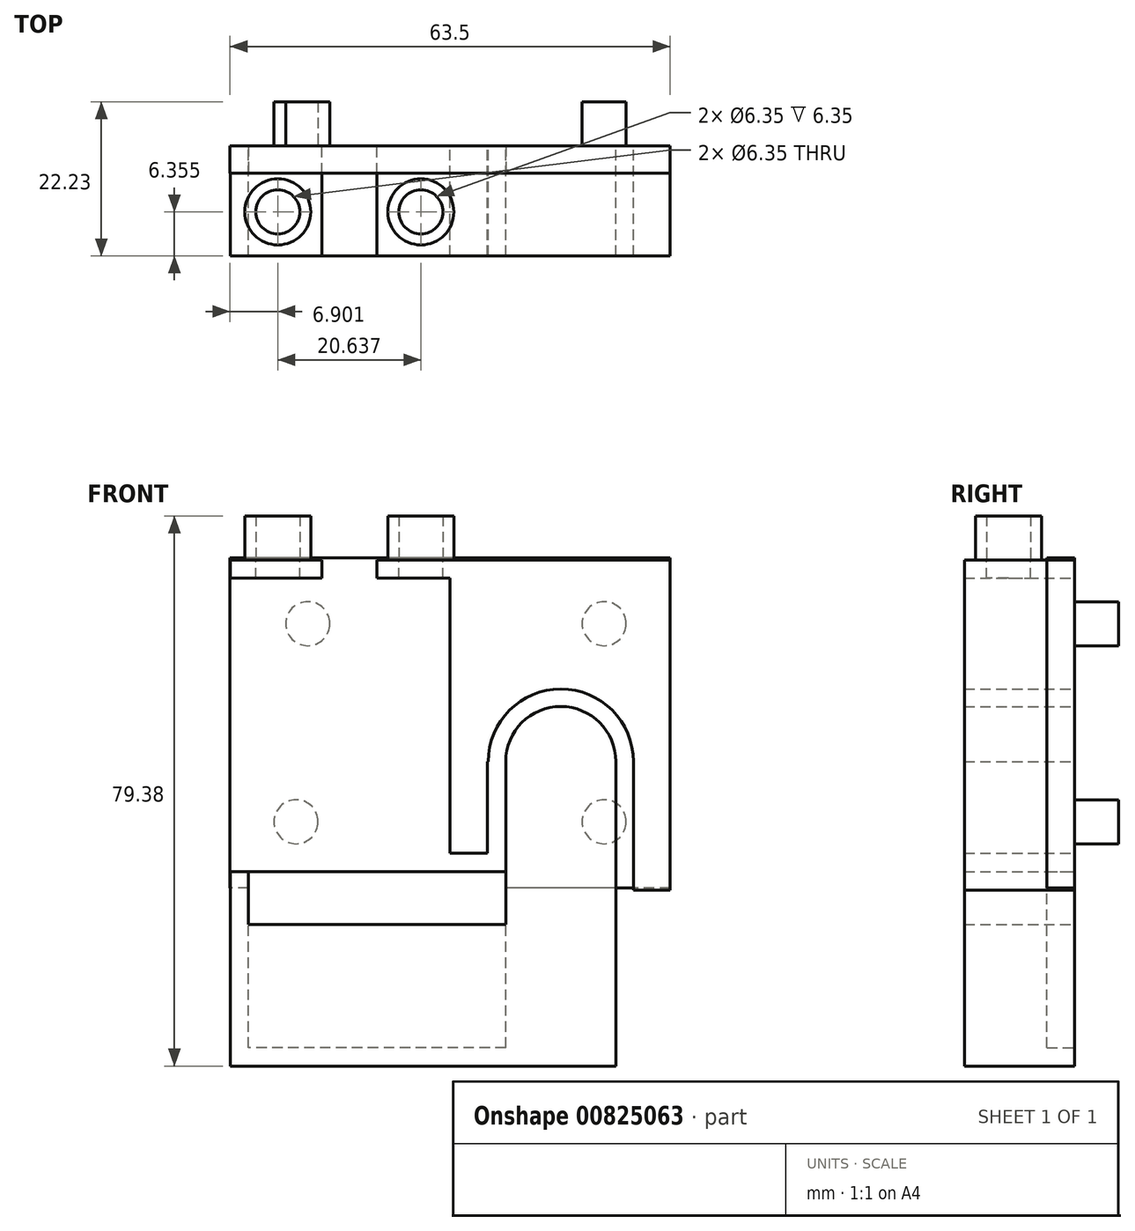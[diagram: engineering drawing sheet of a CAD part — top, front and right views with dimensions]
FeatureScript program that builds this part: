
annotation { "Feature Type Name" : "Feature", "Feature Type Description" : "" }
export const myFeature = defineFeature(function(context is Context, id is Id, definition is map)
    precondition{}
    {
        {
            var Q0;
            Q0=qCreatedBy(makeId("Front.planeOp"),FACE);
            var sketch = newSketch(context, id + "F0", { "sketchPlane" : qUnion([Q0])});
            skLineSegment(sketch, "E0.bottom", {"start": v(-31.75, 44.98) * mm, "end": v(0, 44.98) * mm});
            skLineSegment(sketch, "E0.top", {"start": v(-31.75, 0) * mm, "end": v(0, 0) * mm});
            skLineSegment(sketch, "E0.left", {"start": v(-31.75, 44.98) * mm, "end": v(-31.75, 0) * mm});
            skLineSegment(sketch, "E0.right", {"start": v(0, 44.98) * mm, "end": v(0, 0) * mm});
            skLineSegment(sketch, "E1.bottom", {"start": v(-26.35, 0) * mm, "end": v(-23.7, 0) * mm});
            skLineSegment(sketch, "E1.top", {"start": v(-26.35, 15.88) * mm, "end": v(-23.7, 15.88) * mm});
            skLineSegment(sketch, "E1.left", {"start": v(-26.35, 0) * mm, "end": v(-26.35, 15.87) * mm});
            skLineSegment(sketch, "E1.right", {"start": v(-23.7, 0) * mm, "end": v(-23.7, 15.87) * mm});
            skLineSegment(sketch, "E2.bottom", {"start": v(-7.83, 0) * mm, "end": v(-5.3, 0) * mm});
            skLineSegment(sketch, "E2.top", {"start": v(-7.83, 15.88) * mm, "end": v(-5.3, 15.88) * mm});
            skLineSegment(sketch, "E2.left", {"start": v(-7.83, 0) * mm, "end": v(-7.83, 15.87) * mm});
            skLineSegment(sketch, "E2.right", {"start": v(-5.3, 0) * mm, "end": v(-5.3, 15.87) * mm});
            skArc(sketch, "E3", {"start": v(-5.3, 15.87) * mm, "mid": v(-15.77, 26.35) * mm, "end": v(-26.25, 15.87) * mm});
            skArc(sketch, "E4", {"start": v(-7.83, 15.87) * mm, "mid": v(-15.77, 23.81) * mm, "end": v(-23.7, 15.87) * mm});
            skLineSegment(sketch, "E5.bottom", {"start": v(-26.35, 0) * mm, "end": v(-31.75, 0) * mm});
            skLineSegment(sketch, "E5.top", {"start": v(-26.35, 2.65) * mm, "end": v(-31.75, 2.65) * mm});
            skLineSegment(sketch, "E5.left", {"start": v(-26.35, 0) * mm, "end": v(-26.35, 2.65) * mm});
            skLineSegment(sketch, "E5.right", {"start": v(-31.75, 0) * mm, "end": v(-31.75, 2.65) * mm});
            skLineSegment(sketch, "E6.bottom", {"start": v(-31.75, 44.98) * mm, "end": v(-63.47, 44.98) * mm});
            skLineSegment(sketch, "E6.top", {"start": v(-31.75, 42.34) * mm, "end": v(-63.47, 42.34) * mm});
            skLineSegment(sketch, "E6.left", {"start": v(-31.75, 44.98) * mm, "end": v(-31.75, 42.34) * mm});
            skLineSegment(sketch, "E6.right", {"start": v(-63.47, 44.98) * mm, "end": v(-63.47, 42.34) * mm});
            skLineSegment(sketch, "E7.bottom", {"start": v(-63.47, 42.34) * mm, "end": v(-60.82, 42.34) * mm});
            skLineSegment(sketch, "E7.top", {"start": v(-63.47, 0) * mm, "end": v(-60.82, 0) * mm});
            skLineSegment(sketch, "E7.left", {"start": v(-63.47, 42.34) * mm, "end": v(-63.47, 0) * mm});
            skLineSegment(sketch, "E7.right", {"start": v(-60.82, 42.34) * mm, "end": v(-60.82, 0) * mm});
            skLineSegment(sketch, "E8.bottom", {"start": v(-63.47, 0) * mm, "end": v(0, 0) * mm});
            skLineSegment(sketch, "E8.top", {"start": v(-63.47, -2.65) * mm, "end": v(0, -2.65) * mm});
            skLineSegment(sketch, "E8.left", {"start": v(-63.47, 0) * mm, "end": v(-63.47, -2.65) * mm});
            skLineSegment(sketch, "E8.right", {"start": v(0, 0) * mm, "end": v(0, -2.65) * mm});
            skLineSegment(sketch, "E9.top", {"start": v(-7.83, -2.65) * mm, "end": v(-5.3, -2.65) * mm});
            skLineSegment(sketch, "E9.left", {"start": v(-7.83, 0) * mm, "end": v(-7.83, -2.65) * mm});
            skLineSegment(sketch, "E9.right", {"start": v(-5.3, 0) * mm, "end": v(-5.3, -2.65) * mm});
            skLineSegment(sketch, "E10.bottom", {"start": v(-58.18, 44.98) * mm, "end": v(-55.53, 44.98) * mm});
            skLineSegment(sketch, "E10.top", {"start": v(-58.18, 42.34) * mm, "end": v(-55.53, 42.34) * mm});
            skLineSegment(sketch, "E11.bottom", {"start": v(-50.25, 44.98) * mm, "end": v(-42.31, 44.98) * mm});
            skLineSegment(sketch, "E11.top", {"start": v(-50.25, 42.34) * mm, "end": v(-42.31, 42.34) * mm});
            skLineSegment(sketch, "E11.left", {"start": v(-50.25, 44.98) * mm, "end": v(-50.25, 42.34) * mm});
            skLineSegment(sketch, "E11.right", {"start": v(-42.31, 44.98) * mm, "end": v(-42.31, 42.34) * mm});
            skLineSegment(sketch, "E12.bottom", {"start": v(-37.04, 44.98) * mm, "end": v(-34.4, 44.98) * mm});
            skLineSegment(sketch, "E12.top", {"start": v(-37.04, 42.34) * mm, "end": v(-34.4, 42.34) * mm});
            skSolve(sketch);
        }
        {
            var Q0;
            Q0=makeQuery(id+"F0.imprint","IMPRINT",FACE,{"disambiguationData":[TD([[makeQuery(id+"F0.imprint","IMPRINT",EDGE,{"derivedFrom":sQuery(id+"F0.wireOp",EDGE,"E0.bottom")}),-1.0]])]});
            var Q1;
            {var subQ0=sQuery(id+"F0.wireOp",EDGE,"E1.right");Q1=makeQuery(id+"F0.imprint","IMPRINT",FACE,{"disambiguationData":[TD([[makeQuery(id+"F0.imprint","IMPRINT",EDGE,{"derivedFrom":subQ0}),-1.0]])]});}
            var Q2;
            {var subQ6=sQuery(id+"F0.wireOp",EDGE,"E8.left");Q2=makeQuery(id+"F0.imprint","IMPRINT",FACE,{"disambiguationData":[TD([[makeQuery(id+"F0.imprint","IMPRINT",EDGE,{"derivedFrom":subQ6}),1.0]])]});}
            var Q3;
            {var subQ0=sQuery(id+"F0.wireOp",EDGE,"E8.right");Q3=makeQuery(id+"F0.imprint","IMPRINT",FACE,{"disambiguationData":[TD([[makeQuery(id+"F0.imprint","IMPRINT",EDGE,{"derivedFrom":subQ0}),-1.0]])]});}
            var Q4;
            Q4=makeQuery(id+"F0.imprint","IMPRINT",FACE,{"disambiguationData":[TD([[makeQuery(id+"F0.imprint","IMPRINT",EDGE,{"derivedFrom":sQuery(id+"F0.wireOp",EDGE,"E7.bottom")}),-1.0]])]});
            var Q5;
            {var subQ1=sQuery(id+"F0.wireOp",EDGE,"E6.right");Q5=makeQuery(id+"F0.imprint","IMPRINT",FACE,{"disambiguationData":[TD([[makeQuery(id+"F0.imprint","IMPRINT",EDGE,{"derivedFrom":subQ1}),1.0]])]});}
            var Q6;
            {var subQ0=sQuery(id+"F0.wireOp",EDGE,"E10.right");Q6=makeQuery(id+"F0.imprint","IMPRINT",FACE,{"disambiguationData":[TD([[makeQuery(id+"F0.imprint","IMPRINT",EDGE,{"derivedFrom":subQ0}),1.0]])]});}
            var Q7;
            {var subQ0=sQuery(id+"F0.wireOp",EDGE,"E11.right");Q7=makeQuery(id+"F0.imprint","IMPRINT",FACE,{"disambiguationData":[TD([[makeQuery(id+"F0.imprint","IMPRINT",EDGE,{"derivedFrom":subQ0}),1.0]])]});}
            var Q8;
            {var subQ0=sQuery(id+"F0.wireOp",EDGE,"E6.left");Q8=makeQuery(id+"F0.imprint","IMPRINT",FACE,{"disambiguationData":[TD([[makeQuery(id+"F0.imprint","IMPRINT",EDGE,{"derivedFrom":subQ0}),-1.0]])]});}
            extrude(context, id + "F1", {"entities" : qUnion([Q0, Q1, Q2, Q3, Q4, Q5, Q6, Q7, Q8]), "depth" : 15.88 * mm, "offsetDistance" : 25.4 * mm});
        }
        {
            var Q0;
            Q0=qCreatedBy(makeId("Front.planeOp"),FACE);
            var sketch = newSketch(context, id + "F2", { "sketchPlane" : qUnion([Q0])});
            skLineSegment(sketch, "E13.bottom", {"start": v(0, 45.3) * mm, "end": v(-63.5, 45.3) * mm});
            skLineSegment(sketch, "E13.top", {"start": v(0, -2.33) * mm, "end": v(-63.5, -2.33) * mm});
            skLineSegment(sketch, "E13.left", {"start": v(0, 45.3) * mm, "end": v(0, -2.33) * mm});
            skLineSegment(sketch, "E13.right", {"start": v(-63.5, 45.3) * mm, "end": v(-63.5, -2.33) * mm});
            skCircle(sketch, "E14", {"center": v(-9.53, 35.77) * mm, "radius": 3.18 * mm});
            skCircle(sketch, "E15", {"center": v(-52.28, 35.77) * mm, "radius": 3.18 * mm});
            skCircle(sketch, "E16", {"center": v(-53.97, 7.2) * mm, "radius": 3.18 * mm});
            skCircle(sketch, "E17", {"center": v(-9.52, 7.2) * mm, "radius": 3.18 * mm});
            skSolve(sketch);
        }
        {
            var Q0;
            Q0=qSketchRegion(id+"F2",true);
            var Q1;
            Q1=makeQuery(id+"F2.imprint","IMPRINT",FACE,{"disambiguationData":[TD([[makeQuery(id+"F2.imprint","IMPRINT",EDGE,{"derivedFrom":sQuery(id+"F2.wireOp",EDGE,"E15")}),1.0]])]});
            var Q2;
            Q2=makeQuery(id+"F2.imprint","IMPRINT",FACE,{"disambiguationData":[TD([[makeQuery(id+"F2.imprint","IMPRINT",EDGE,{"derivedFrom":sQuery(id+"F2.wireOp",EDGE,"E16")}),1.0]])]});
            var Q3;
            Q3=makeQuery(id+"F2.imprint","IMPRINT",FACE,{"disambiguationData":[TD([[makeQuery(id+"F2.imprint","IMPRINT",EDGE,{"derivedFrom":sQuery(id+"F2.wireOp",EDGE,"E17")}),1.0]])]});
            var Q4;
            Q4=makeQuery(id+"F2.imprint","IMPRINT",FACE,{"disambiguationData":[TD([[makeQuery(id+"F2.imprint","IMPRINT",EDGE,{"derivedFrom":sQuery(id+"F2.wireOp",EDGE,"E14")}),1.0]])]});
            extrude(context, id + "F3", {"entities" : qUnion([Q0, Q1, Q2, Q3, Q4]), "depth" : 3.97 * mm, "offsetDistance" : 25.4 * mm});
        }
        {
            var Q0;
            Q0=makeQuery(id+"F2.imprint","IMPRINT",FACE,{"disambiguationData":[TD([[makeQuery(id+"F2.imprint","IMPRINT",EDGE,{"derivedFrom":sQuery(id+"F2.wireOp",EDGE,"E14")}),1.0]])]});
            var Q1;
            Q1=makeQuery(id+"F2.imprint","IMPRINT",FACE,{"disambiguationData":[TD([[makeQuery(id+"F2.imprint","IMPRINT",EDGE,{"derivedFrom":sQuery(id+"F2.wireOp",EDGE,"E15")}),1.0]])]});
            var Q2;
            Q2=makeQuery(id+"F2.imprint","IMPRINT",FACE,{"disambiguationData":[TD([[makeQuery(id+"F2.imprint","IMPRINT",EDGE,{"derivedFrom":sQuery(id+"F2.wireOp",EDGE,"E17")}),1.0]])]});
            var Q3;
            Q3=makeQuery(id+"F2.imprint","IMPRINT",FACE,{"disambiguationData":[TD([[makeQuery(id+"F2.imprint","IMPRINT",EDGE,{"derivedFrom":sQuery(id+"F2.wireOp",EDGE,"E16")}),1.0]])]});
            var Q4;
            Q4=sQuery(id+"F2.wireOp",EDGE,"E14");
            var Q5;
            Q5=sQuery(id+"F2.wireOp",EDGE,"E15");
            var Q6;
            Q6=sQuery(id+"F2.wireOp",EDGE,"E17");
            var Q7;
            Q7=sQuery(id+"F2.wireOp",EDGE,"E16");
            extrude(context, id + "F4", {"entities" : qUnion([Q0, Q1, Q2, Q3]), "surfaceEntities" : qUnion([Q4, Q5, Q6, Q7]), "oppositeDirection" : true, "depth" : 6.35 * mm, "offsetDistance" : 25.4 * mm});
        }
        {
            var Q0;
            Q0=makeQuery(id+"F1.opExtrude","SWEPT_FACE",FACE,{"disambiguationData":[OSD([sQuery(id+"F0.wireOp",EDGE,"E6.bottom"),sQuery(id+"F0.wireOp",EDGE,"E10.bottom")])]});
            var sketch = newSketch(context, id + "F5", { "sketchPlane" : qUnion([Q0])});
            skCircle(sketch, "E18", {"center": v(-56.6, -9.52) * mm, "radius": 3.18 * mm});
            skCircle(sketch, "E19", {"center": v(-35.96, -9.52) * mm, "radius": 3.18 * mm});
            skCircle(sketch, "E20", {"center": v(-56.6, -9.52) * mm, "radius": 4.76 * mm});
            skCircle(sketch, "E21", {"center": v(-35.96, -9.52) * mm, "radius": 4.76 * mm});
            skSolve(sketch);
        }
        {
            var Q0;
            Q0=qSketchRegion(id+"F5",true);
            extrude(context, id + "F6", {"entities" : qUnion([Q0]), "depth" : 6.35 * mm, "offsetDistance" : 25.4 * mm});
        }
        {
            var Q0;
            Q0=makeQuery(id+"F1.opExtrude","SWEPT_FACE",FACE,{"disambiguationData":[OSD([sQuery(id+"F0.wireOp",EDGE,"E6.bottom"),sQuery(id+"F0.wireOp",EDGE,"E10.bottom")])]});
            var sketch = newSketch(context, id + "F7", { "sketchPlane" : qUnion([Q0])});
            skCircle(sketch, "E22", {"center": v(-35.96, -9.52) * mm, "radius": 3.18 * mm});
            skCircle(sketch, "E23", {"center": v(-56.6, -9.52) * mm, "radius": 3.18 * mm});
            skSolve(sketch);
        }
        {
            var Q0;
            Q0=qSketchRegion(id+"F7",true);
            extrude(context, id + "F8", {"entities" : qUnion([Q0]), "operationType" : NewBodyOperationType.REMOVE, "oppositeDirection" : true, "depth" : 25.4 * mm, "offsetDistance" : 25.4 * mm});
        }
        {
            var Q0;
            {var subQ0=sQuery(id+"F0.wireOp",EDGE,"E8.top");Q0=makeQuery(id+"F1.opExtrude","SWEPT_FACE",FACE,{"disambiguationData":[OSD([subQ0]),TDD([makeQuery(id+"F0.imprint","IMPRINT",EDGE,{"disambiguationData":[TD([[makeQuery(id+"F0.imprint","INTERSECT",VERTEX,{"derivedFrom":[subQ0,sQuery(id+"F0.wireOp",EDGE,"E8.left")]}),-1.0]])],"derivedFrom":subQ0})])]});}
            var sketch = newSketch(context, id + "F9", { "sketchPlane" : qUnion([Q0])});
            skLineSegment(sketch, "E24.bottom", {"start": v(-63.47, 0) * mm, "end": v(-7.83, 0) * mm});
            skLineSegment(sketch, "E24.top", {"start": v(-63.47, 15.88) * mm, "end": v(-7.83, 15.88) * mm});
            skLineSegment(sketch, "E24.left", {"start": v(-63.47, 0) * mm, "end": v(-63.47, 15.88) * mm});
            skLineSegment(sketch, "E24.right", {"start": v(-7.83, 0) * mm, "end": v(-7.83, 15.88) * mm});
            skSolve(sketch);
        }
        {
            var Q0;
            Q0=qSketchRegion(id+"F9",true);
            extrude(context, id + "F10", {"entities" : qUnion([Q0]), "operationType" : NewBodyOperationType.ADD, "depth" : 25.4 * mm, "offsetDistance" : 25.4 * mm});
        }
        {
            var Q0;
            {var subQ0=sQuery(id+"F0.wireOp",EDGE,"E8.bottom");var subQ1=makeQuery(id+"F0.imprint","INTERSECT",VERTEX,{"derivedFrom":[sQuery(id+"F0.wireOp",EDGE,"E5.left"),subQ0]});var subQ2=makeQuery(id+"F0.imprint","INTERSECT",VERTEX,{"derivedFrom":[sQuery(id+"F0.wireOp",EDGE,"E5.right"),subQ0]});Q0=makeQuery(id+"F1.opExtrude","SWEPT_FACE",FACE,{"disambiguationData":[OSD([subQ0]),TDD([makeQuery(id+"F0.imprint","IMPRINT",EDGE,{"disambiguationData":[TD([[subQ2,1.0]])],"derivedFrom":subQ0}),makeQuery(id+"F0.imprint","IMPRINT",EDGE,{"disambiguationData":[TD([[subQ1,1.0]])],"derivedFrom":subQ0}),makeQuery(id+"F0.imprint","IMPRINT",EDGE,{"disambiguationData":[TD([[makeQuery(id+"F0.imprint","INTERSECT",VERTEX,{"derivedFrom":[sQuery(id+"F0.wireOp",EDGE,"E1.right"),subQ0]}),1.0]])],"derivedFrom":subQ0})])]});}
            var sketch = newSketch(context, id + "F11", { "sketchPlane" : qUnion([Q0])});
            skLineSegment(sketch, "E25.bottom", {"start": v(-60.82, -15.88) * mm, "end": v(-23.7, -15.88) * mm});
            skLineSegment(sketch, "E25.top", {"start": v(-60.82, 0) * mm, "end": v(-23.7, 0) * mm});
            skLineSegment(sketch, "E25.left", {"start": v(-60.82, -15.88) * mm, "end": v(-60.82, 0) * mm});
            skLineSegment(sketch, "E25.right", {"start": v(-23.7, -15.88) * mm, "end": v(-23.7, 0) * mm});
            skSolve(sketch);
        }
        {
            var Q0;
            Q0=qSketchRegion(id+"F11",true);
            extrude(context, id + "F12", {"entities" : qUnion([Q0]), "operationType" : NewBodyOperationType.REMOVE, "oppositeDirection" : true, "depth" : 7.62 * mm, "offsetDistance" : 25.4 * mm});
        }
        {
            var Q0;
            Q0=makeQuery(id+"F12.boolean.opBoolean","COPY",FACE,{"derivedFrom":makeQuery(id+"F12.opExtrude","CAP_FACE",FACE,{"disambiguationData":[OSD([sQuery(id+"F11.wireOp",EDGE,"E25.bottom"),sQuery(id+"F11.wireOp",EDGE,"E25.top"),sQuery(id+"F11.wireOp",EDGE,"E25.left"),sQuery(id+"F11.wireOp",EDGE,"E25.right")])],"isStart":true})});
            var sketch = newSketch(context, id + "F13", { "sketchPlane" : qUnion([Q0])});
            skLineSegment(sketch, "E26.bottom", {"start": v(-60.82, 3.97) * mm, "end": v(-23.7, 3.97) * mm});
            skLineSegment(sketch, "E26.top", {"start": v(-60.82, 0) * mm, "end": v(-23.7, 0) * mm});
            skLineSegment(sketch, "E26.left", {"start": v(-60.82, 3.97) * mm, "end": v(-60.82, 0) * mm});
            skLineSegment(sketch, "E26.right", {"start": v(-23.7, 3.97) * mm, "end": v(-23.7, 0) * mm});
            skSolve(sketch);
        }
        {
            var Q0;
            Q0=qSketchRegion(id+"F13",true);
            extrude(context, id + "F14", {"entities" : qUnion([Q0]), "depth" : 25.4 * mm, "offsetDistance" : 25.4 * mm});
        }
    });
